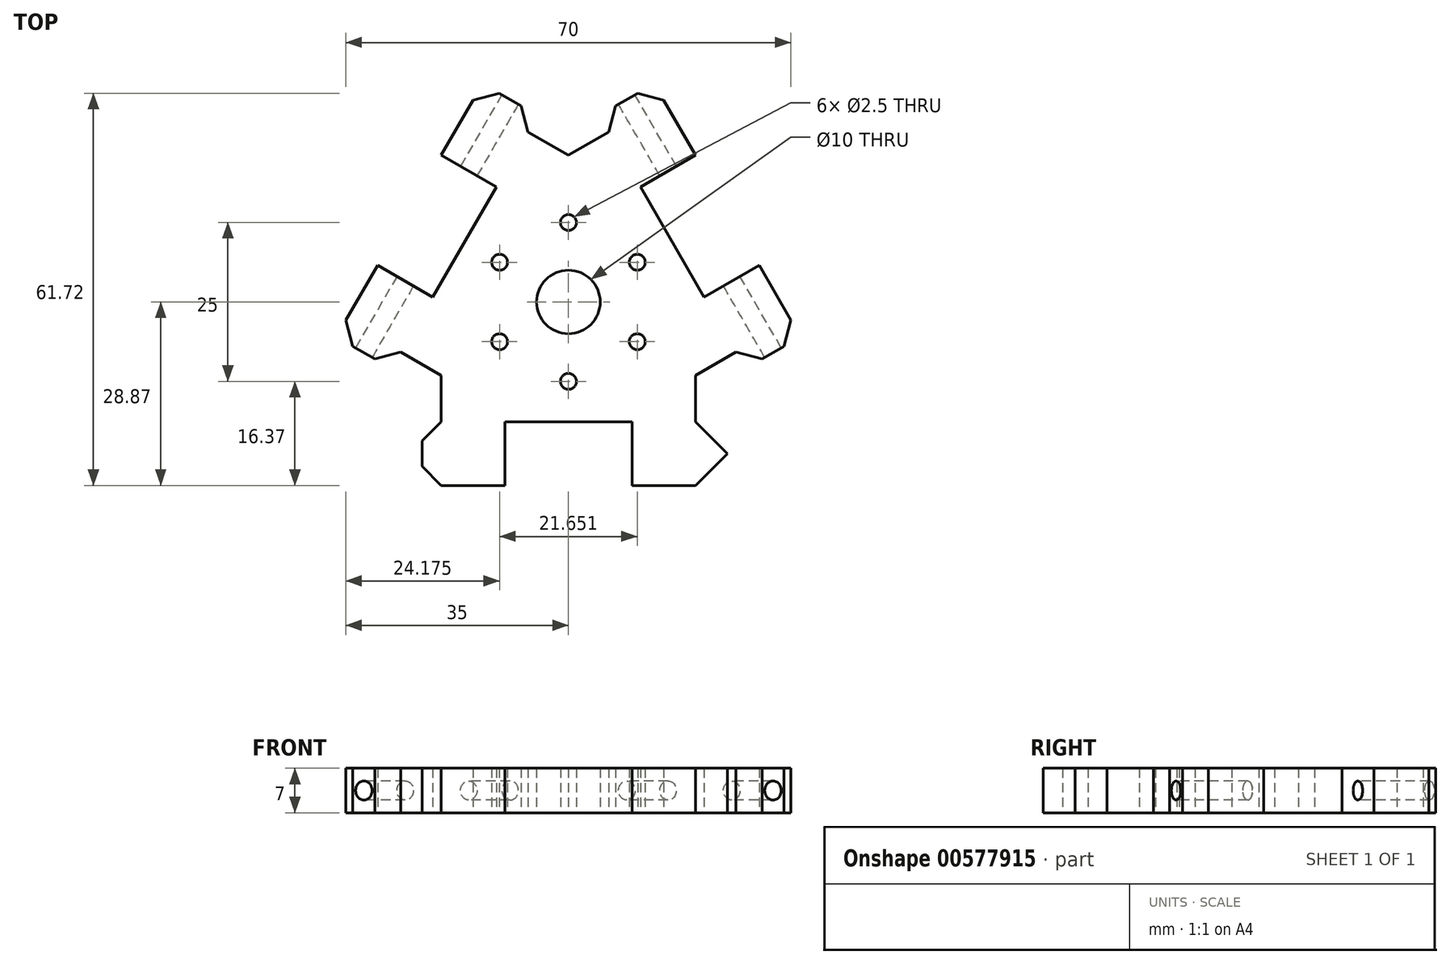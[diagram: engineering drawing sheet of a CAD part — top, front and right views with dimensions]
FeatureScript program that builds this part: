
annotation { "Feature Type Name" : "Feature", "Feature Type Description" : "" }
export const myFeature = defineFeature(function(context is Context, id is Id, definition is map)
    precondition{}
    {
        {
            var Q0;
            Q0=qCreatedBy(makeId("Top.planeOp"),FACE);
            var sketch = newSketch(context, id + "F0", { "sketchPlane" : qUnion([Q0])});
            skLineSegment(sketch, "E0", {"start": v(-20, -28.87) * mm, "end": v(-10, -28.87) * mm});
            skPoint(sketch, "E1", {"position": v(0, 0) * mm});
            skLineSegment(sketch, "E2", {"start": v(-10, -18.87) * mm, "end": v(10, -18.87) * mm});
            skLineSegment(sketch, "E3", {"start": v(-21.34, 0.77) * mm, "end": v(-11.34, 18.1) * mm});
            skCircle(sketch, "E4", {"center": v(0, 0) * mm, "radius": 5 * mm});
            skLineSegment(sketch, "E5", {"start": v(11.34, 18.1) * mm, "end": v(20, 23.1) * mm});
            skLineSegment(sketch, "E6", {"start": v(21.34, 0.77) * mm, "end": v(30, 5.77) * mm});
            skLineSegment(sketch, "E7", {"start": v(10, -18.87) * mm, "end": v(10, -28.87) * mm});
            skLineSegment(sketch, "E8", {"start": v(-10, -18.87) * mm, "end": v(-10, -28.87) * mm});
            skLineSegment(sketch, "E9", {"start": v(-20, 23.1) * mm, "end": v(-11.34, 18.1) * mm});
            skLineSegment(sketch, "E10", {"start": v(-20, -18.87) * mm, "end": v(-20, -11.55) * mm});
            skLineSegment(sketch, "E11", {"start": v(-20, -11.55) * mm, "end": v(-26.34, -7.89) * mm});
            skLineSegment(sketch, "E12", {"start": v(20, -18.87) * mm, "end": v(20, -11.55) * mm});
            skLineSegment(sketch, "E13", {"start": v(20, -11.55) * mm, "end": v(26.34, -7.89) * mm});
            skLineSegment(sketch, "E14", {"start": v(6.34, 26.75) * mm, "end": v(0, 23.1) * mm});
            skLineSegment(sketch, "E15", {"start": v(0, 23.1) * mm, "end": v(-6.34, 26.75) * mm});
            skLineSegment(sketch, "E16", {"start": v(-33.9, -6.98) * mm, "end": v(-30.44, -8.98) * mm});
            skLineSegment(sketch, "E17", {"start": v(-23, -21.87) * mm, "end": v(-23, -25.87) * mm});
            skLineSegment(sketch, "E18", {"start": v(23, -25.87) * mm, "end": v(23, -21.87) * mm});
            skLineSegment(sketch, "E19", {"start": v(30.44, -8.98) * mm, "end": v(33.9, -6.98) * mm});
            skLineSegment(sketch, "E20", {"start": v(7.44, 30.85) * mm, "end": v(10.9, 32.85) * mm});
            skLineSegment(sketch, "E21", {"start": v(-7.44, 30.85) * mm, "end": v(-10.9, 32.85) * mm});
            skCircle(sketch, "E22", {"center": v(-10.83, 6.25) * mm, "radius": 1.25 * mm});
            skCircle(sketch, "E23", {"center": v(0, 12.5) * mm, "radius": 1.25 * mm});
            skCircle(sketch, "E24", {"center": v(0, -12.5) * mm, "radius": 1.25 * mm});
            skCircle(sketch, "E25", {"center": v(-10.83, -6.25) * mm, "radius": 1.25 * mm});
            skCircle(sketch, "E26", {"center": v(10.83, -6.25) * mm, "radius": 1.25 * mm});
            skCircle(sketch, "E27", {"center": v(10.83, 6.25) * mm, "radius": 1.25 * mm});
            skLineSegment(sketch, "E28", {"start": v(-26.34, -7.89) * mm, "end": v(-30.44, -8.98) * mm});
            skLineSegment(sketch, "E29", {"start": v(-35, -2.89) * mm, "end": v(-33.9, -6.98) * mm});
            skLineSegment(sketch, "E30", {"start": v(-15, 31.75) * mm, "end": v(-10.9, 32.85) * mm});
            skLineSegment(sketch, "E31", {"start": v(-6.34, 26.75) * mm, "end": v(-7.44, 30.85) * mm});
            skLineSegment(sketch, "E32", {"start": v(6.34, 26.75) * mm, "end": v(7.44, 30.85) * mm});
            skLineSegment(sketch, "E33", {"start": v(15, 31.75) * mm, "end": v(10.9, 32.85) * mm});
            skLineSegment(sketch, "E34", {"start": v(26.34, -7.89) * mm, "end": v(30.44, -8.98) * mm});
            skLineSegment(sketch, "E35", {"start": v(35, -2.89) * mm, "end": v(33.9, -6.98) * mm});
            skLineSegment(sketch, "E36", {"start": v(20, -18.87) * mm, "end": v(23, -21.87) * mm});
            skLineSegment(sketch, "E37", {"start": v(20, -28.87) * mm, "end": v(23, -25.87) * mm});
            skLineSegment(sketch, "E38", {"start": v(-20, -28.87) * mm, "end": v(-23, -25.87) * mm});
            skLineSegment(sketch, "E39", {"start": v(-20, -18.87) * mm, "end": v(-23, -21.87) * mm});
            skLineSegment(sketch, "E40.trimOffspring", {"start": v(-15, 31.75) * mm, "end": v(-20, 23.1) * mm});
            skPoint(sketch, "E41.orphan", {"position": v(0, 57.74) * mm});
            skLineSegment(sketch, "E42.trimOffspring", {"start": v(20, 23.1) * mm, "end": v(15, 31.75) * mm});
            skLineSegment(sketch, "E43.trimOffspring", {"start": v(35, -2.89) * mm, "end": v(30, 5.77) * mm});
            skLineSegment(sketch, "E44.trimOffspring", {"start": v(21.34, 0.77) * mm, "end": v(11.34, 18.1) * mm});
            skLineSegment(sketch, "E45.trimOffspring", {"start": v(10, -28.87) * mm, "end": v(20, -28.87) * mm});
            skLineSegment(sketch, "E46", {"start": v(-35, -2.89) * mm, "end": v(-30, 5.77) * mm});
            skLineSegment(sketch, "E47", {"start": v(-30, 5.77) * mm, "end": v(-21.34, 0.77) * mm});
            skLineSegment(sketch, "E48", {"start": v(25, -23.87) * mm, "end": v(23, -25.87) * mm});
            skLineSegment(sketch, "E49", {"start": v(23, -21.87) * mm, "end": v(25, -23.87) * mm});
            skLineSegment(sketch, "E50", {"start": v(20, -18.87) * mm, "end": v(20, -28.87) * mm});
            skSolve(sketch);
        }
        {
            var Q0;
            Q0=makeQuery(id+"F0.imprint","IMPRINT",FACE,{"disambiguationData":[TD([[makeQuery(id+"F0.imprint","IMPRINT",EDGE,{"derivedFrom":sQuery(id+"F0.wireOp",EDGE,"E0")}),1.0]])]});
            var Q1;
            Q1=makeQuery(id+"F0.imprint","IMPRINT",FACE,{"disambiguationData":[TD([[makeQuery(id+"F0.imprint","IMPRINT",EDGE,{"derivedFrom":sQuery(id+"F0.wireOp",EDGE,"E18")}),-1.0]])]});
            var Q2;
            Q2=makeQuery(id+"F0.imprint","IMPRINT",FACE,{"disambiguationData":[TD([[makeQuery(id+"F0.imprint","IMPRINT",EDGE,{"derivedFrom":sQuery(id+"F0.wireOp",EDGE,"E18")}),1.0]])]});
            extrude(context, id + "F1", {"entities" : qUnion([Q0, Q1, Q2]), "depth" : 7 * mm, "offsetDistance" : 25 * mm});
        }
        {
            var Q0;
            Q0=makeQuery(id+"F1.opExtrude","SWEPT_FACE",FACE,{"disambiguationData":[OSD([sQuery(id+"F0.wireOp",EDGE,"E16")])]});
            var sketch = newSketch(context, id + "F2", { "sketchPlane" : qUnion([Q0])});
            skCircle(sketch, "E51", {"center": v(-23.87, 3.5) * mm, "radius": 1.5 * mm});
            skPoint(sketch, "E51.centerSnap0", {"position": v(-21.87, 3.5) * mm});
            skPoint(sketch, "E51.centerSnap1", {"position": v(-23.87, 7) * mm});
            skSolve(sketch);
        }
        {
            var Q0;
            Q0=makeQuery(id+"F2.imprint","IMPRINT",FACE,{"disambiguationData":[TD([[makeQuery(id+"F2.imprint","IMPRINT",EDGE,{"derivedFrom":sQuery(id+"F2.wireOp",EDGE,"E51")}),1.0]])]});
            extrude(context, id + "F3", {"entities" : qUnion([Q0]), "operationType" : NewBodyOperationType.REMOVE, "oppositeDirection" : true, "depth" : 46 * mm, "offsetDistance" : 25 * mm});
        }
        {
            var Q0;
            Q0=makeQuery(id+"F1.opExtrude","SWEPT_FACE",FACE,{"disambiguationData":[OSD([sQuery(id+"F0.wireOp",EDGE,"E20")])]});
            var sketch = newSketch(context, id + "F4", { "sketchPlane" : qUnion([Q0])});
            skCircle(sketch, "E52", {"center": v(-23.87, 3.5) * mm, "radius": 1.5 * mm});
            skPoint(sketch, "E52.centerSnap0", {"position": v(-21.87, 3.5) * mm});
            skPoint(sketch, "E52.centerSnap1", {"position": v(-23.87, 7) * mm});
            skSolve(sketch);
        }
        {
            var Q0;
            Q0=makeQuery(id+"F4.imprint","IMPRINT",FACE,{"disambiguationData":[TD([[makeQuery(id+"F4.imprint","IMPRINT",EDGE,{"derivedFrom":sQuery(id+"F4.wireOp",EDGE,"E52")}),1.0]])]});
            extrude(context, id + "F5", {"entities" : qUnion([Q0]), "operationType" : NewBodyOperationType.REMOVE, "oppositeDirection" : true, "depth" : 46 * mm, "offsetDistance" : 25 * mm});
        }
        {
            var Q0;
            Q0=makeQuery(id+"F1.opExtrude","SWEPT_FACE",FACE,{"disambiguationData":[OSD([sQuery(id+"F0.wireOp",EDGE,"E37"),sQuery(id+"F0.wireOp",EDGE,"E48")])]});
            var sketch = newSketch(context, id + "F6", { "sketchPlane" : qUnion([Q0])});
            skLineSegment(sketch, "E53", {"start": v(-6.27, 7) * mm, "end": v(0.8, 3.5) * mm});
            skLineSegment(sketch, "E54", {"start": v(0.8, 3.5) * mm, "end": v(-6.27, 0) * mm});
            skSolve(sketch);
        }
        {
            var Q0;
            Q0=sQuery(id+"F6.wireOp",VERTEX,"E54.start");
            var Q1;
            Q1=qCreatedBy(makeId("Right.planeOp"),FACE);
            cPlane(context, id + "F7", {"entities" : qUnion([Q0, Q1]), "cplaneType" : CPlaneType.PLANE_POINT, "offset" : 25 * mm, "width" : 150 * mm, "height" : 150 * mm});
        }
    });
